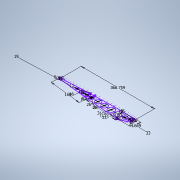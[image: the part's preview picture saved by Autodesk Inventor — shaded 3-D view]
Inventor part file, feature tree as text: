
AUTODESK INVENTOR PART (.ipt)
format: ipt  version: 2022 (Build 260153000, 153)  size: 207,872 bytes
history: native  units: mm
features: sketch x1
ambient origin geometry x8: Origin, YZ Plane, XZ Plane, XY Plane, X Axis, Y Axis, Z Axis, Center Point
feature tree (1):
  sketch  "Sketch1"  dims[d8=159.921431mm d26=5.0mm d27=5.0mm d31=34.456mm d36=5.0mm d37=5.0mm d50=368.759386mm d52=28.0mm d53=31.0mm d54=26.0mm d57=16.0mm d59=33.0mm d65=44.669323mm d66=20.0mm d67=12.0mm d68=160.0mm d69=8.0mm d70=23.0mm d71=8.0mm d73=16.0mm d77=2.0mm d78=33.0mm d79=8.0mm d80=19.0mm d81=16.0mm d82=1.0mm d83=1.0mm d84=1.0mm d85=1.0mm d86=1.0mm d87=0.8mm d88=1.0mm d89=19.0mm d90=19.0mm]
